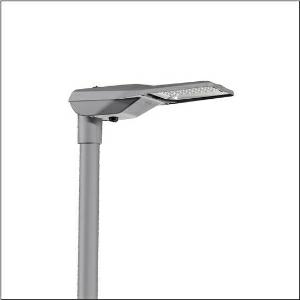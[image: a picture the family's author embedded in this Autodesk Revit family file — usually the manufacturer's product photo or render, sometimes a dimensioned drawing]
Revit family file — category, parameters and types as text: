
# Revit family: streetlight_sl_21_iq_mini___stw1_0a_5xe2e31y08jb_3a8f
name_source: partatom
category: Lighting Fixtures
units: mm (PartAtom-declared; Revit-internal decimal feet)

## family parameters
Cut with Voids When Loaded = No
Host = Face
Light Source = No
Part Type = Normal
Room Calculation Point = No
Round Connector Dimension = Use Diameter
Shared = No

## types (1)
- --- (1 x LED, 11210 lm, 72.5 W, 3000K)
    Apparent Load = 73 VA
    CIE Flux Codes = 39 75 98 100 100
    Color Rendering = 70
    Color Temperature = 3000K
    Default Elevation = 1800 mm
    Description = Streetlight SL 21 iQ mini, mast luminaire, primary light control with lens, of PMMA, primary optical cover: cover, of toughened safety glass, transparent, light distribution: STW1.0a, light emission: direct distribution, primary light characteristic: asymmetric, installation type: post-top, side-entry, LED, High Power LED, rated luminous flux: 11.210lm, luminous efficacy: 155lm/W, light colour: 730, colour temperature: 3000K, control gear: iQ-Street Remote, D4i with power reduction, control: pre-setting: logarithmic dimming characteristic, Street-Remote, Auto-Match, Temp-Guard, Lumen-Switch, Night-Set, Smart-Wire, Light-Fading, Desk-Remote (wireless, voltage-free reading and setting of iQ features in the workshop via application-optimized NFC function/RFID function), optimised constant luminous flux control (CLO 2.0), mains connection: 220..240V, AC, 50/60Hz, start of lifetime: 73W, end of service life: 76W, reduction: 33W, luminaire housing, of diecast aluminium, powder-coated, Siteco® metallic grey (DB 702S), corrosivity category C5 mid according to DIN EN ISO 12944, please order mast flange separately, inclination adjustable: 0°, 5°, 10°, 15°, sealing non-destructively replaceable, multi-level sealing system, length: 628mm, width: 235mm, height: 110mm, mast flange for spigot size: 42mm (side-entry): 5XC10008XM4, 60/48mm (side-entry/post-top): 5XC10108XM2, 76/60mm (side-entry/post-top): 5XC10108XM1, mounting height: 4..8m, Smart Interface below and above, protection rating (complete): IP66, insulation class (complete): insulation class II (safety insulation), certification: CE, ENEC, ENEC+, VDE, impact resistance: IK10, permissible operating ambient temperature for outdoor applications: -40..+50°C, standard-compliant lighting for roads and squares, packaging unit: 1 piece

Light Distribution: STW1.0a
    Height = 110 mm
    Lamp = 1 x LED
    Lamp Light Flux = 11210 lm
    Lamp Power = 72.5 W
    Lamp count = 1
    Length = 625 mm
    Luminous efficacy = 155 lm/W
    Manufacturer = Siteco
    ModVariant = No
    Model = 5XE2E31Y08JB
    Number of Poles = 1
    OnlyDefault = Yes
    Power Factor = 1
    Product Name = Streetlight SL 21 iQ mini | STW1.0a
    Product group = mast luminaire | pylon top
    ProductGroupID = 6100
    Protection Class = Protection class II
    Protection Degree = IP 66
    RLX_Detail_Level = 1
    RLX_Emergency_Light_Flux = 0 lm
    RLX_Emergency_Type = 0
    RLX_Emergency_Type_DB = No
    RlxData = <blob elided: 26765 chars, md5=ce9c8662>
    Socket = socket
    Standby Power = 0 W
    System Light Flux = 11210 lm
    System Power = 73 W
    Type Comments = factory setting: luminous flux: 100 % | dim-lin: 254 | 755 mA
    Type Image = l_1003514.jpg
    URL = http://relux.com
    VarID = @adj_113692
    Voltage = 0 V
    Weight = 0.00 kg
    Width = 234 mm

## geometry (parser evidence)
native form markers: Blend x4, Sweep x10
no freeform markers — native parametric forms only
